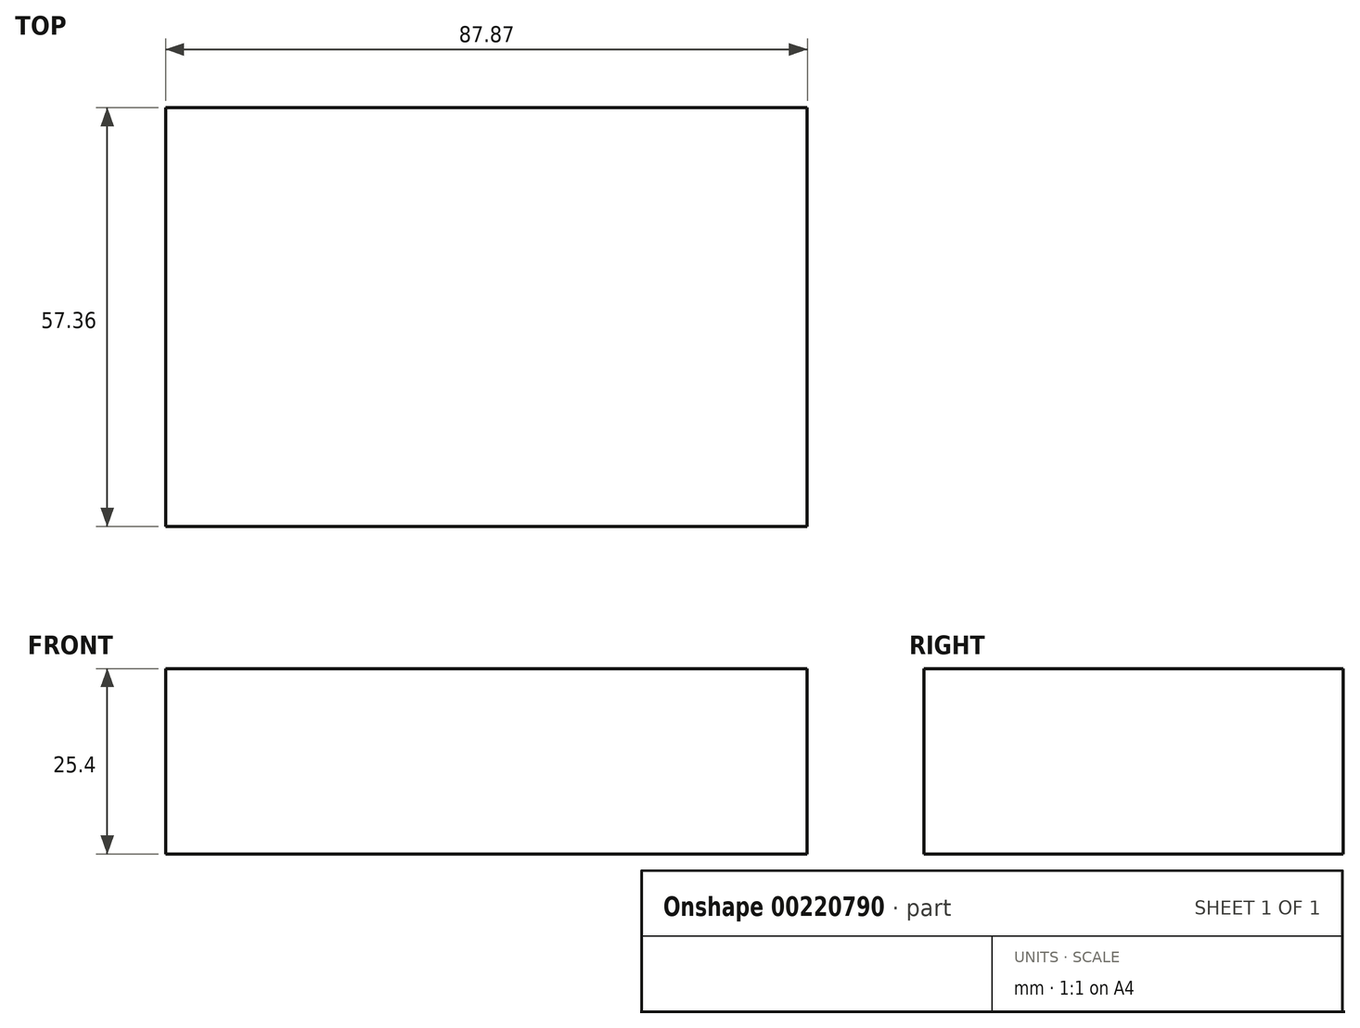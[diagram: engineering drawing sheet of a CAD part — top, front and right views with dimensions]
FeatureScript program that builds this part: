
annotation { "Feature Type Name" : "Feature", "Feature Type Description" : "" }
export const myFeature = defineFeature(function(context is Context, id is Id, definition is map)
    precondition{}
    {
        {
            var Q0;
            Q0=qCreatedBy(makeId("Top.planeOp"),FACE);
            var sketch = newSketch(context, id + "F0", { "sketchPlane" : qUnion([Q0])});
            skLineSegment(sketch, "E0.bottom", {"start": v(-32.57, 7.15) * mm, "end": v(55.3, 7.15) * mm});
            skLineSegment(sketch, "E0.top", {"start": v(-32.57, -50.2) * mm, "end": v(55.3, -50.2) * mm});
            skLineSegment(sketch, "E0.left", {"start": v(-32.57, 7.15) * mm, "end": v(-32.57, -50.2) * mm});
            skLineSegment(sketch, "E0.right", {"start": v(55.3, 7.15) * mm, "end": v(55.3, -50.2) * mm});
            skSolve(sketch);
        }
        {
            var Q0;
            Q0 = qSketchRegion(id + "F0", true);
            extrude(context, id + "F1", {"entities" : qUnion([Q0]), "depth" : 25.4 * mm});
        }
    });
